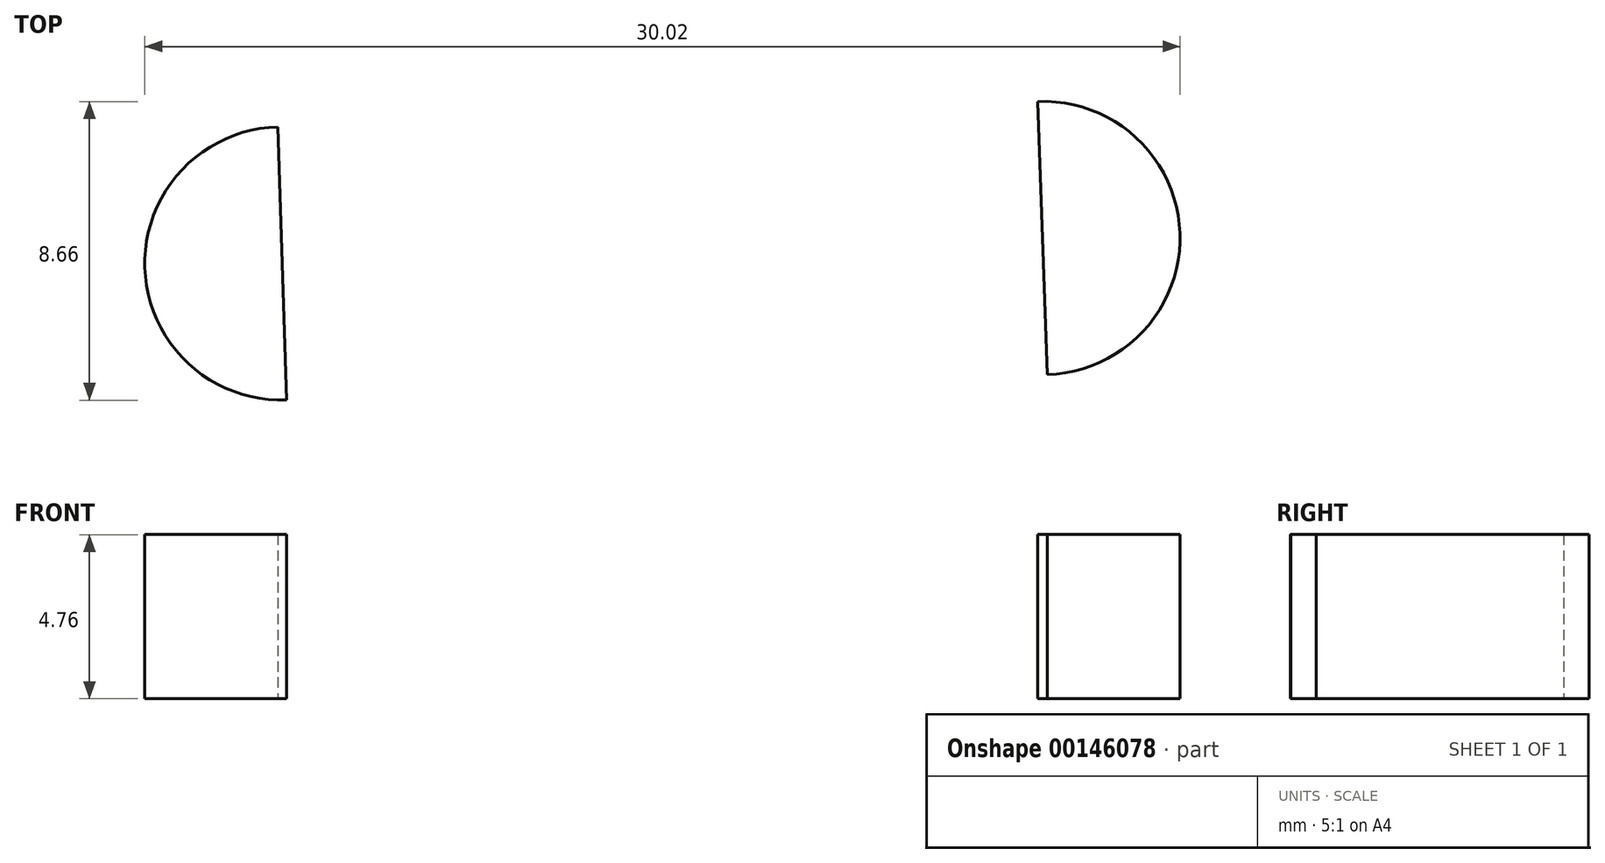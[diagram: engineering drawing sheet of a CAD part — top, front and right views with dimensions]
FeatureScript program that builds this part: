
annotation { "Feature Type Name" : "Feature", "Feature Type Description" : "" }
export const myFeature = defineFeature(function(context is Context, id is Id, definition is map)
    precondition{}
    {
        {
            var Q0;
            Q0=qCreatedBy(makeId("Top.planeOp"),FACE);
            var sketch = newSketch(context, id + "F0", { "sketchPlane" : qUnion([Q0])});
            skArc(sketch, "E0", {"start": v(-31, -7.91) * mm, "mid": v(-27.15, -3.82) * mm, "end": v(-31.28, 0) * mm});
            skLineSegment(sketch, "E1", {"start": v(-31.28, 0) * mm, "end": v(-31, -7.91) * mm});
            skLineSegment(sketch, "E2", {"start": v(-42.4, 2.97) * mm, "end": v(-41.7, -18.31) * mm});
            skLineSegment(sketch, "E3.MirrorCS", {"start": v(-53.3, -0.74) * mm, "end": v(-53.06, -8.65) * mm});
            skArc(sketch, "E4.MirrorCS", {"start": v(-53.06, -8.65) * mm, "mid": v(-57.17, -4.82) * mm, "end": v(-53.3, -0.74) * mm});
            skSolve(sketch);
        }
        {
            var Q0;
            Q0 = qSketchRegion(id + "F0", true);
            extrude(context, id + "F1", {"entities" : qUnion([Q0]), "depth" : 4.76 * mm});
        }
    });
